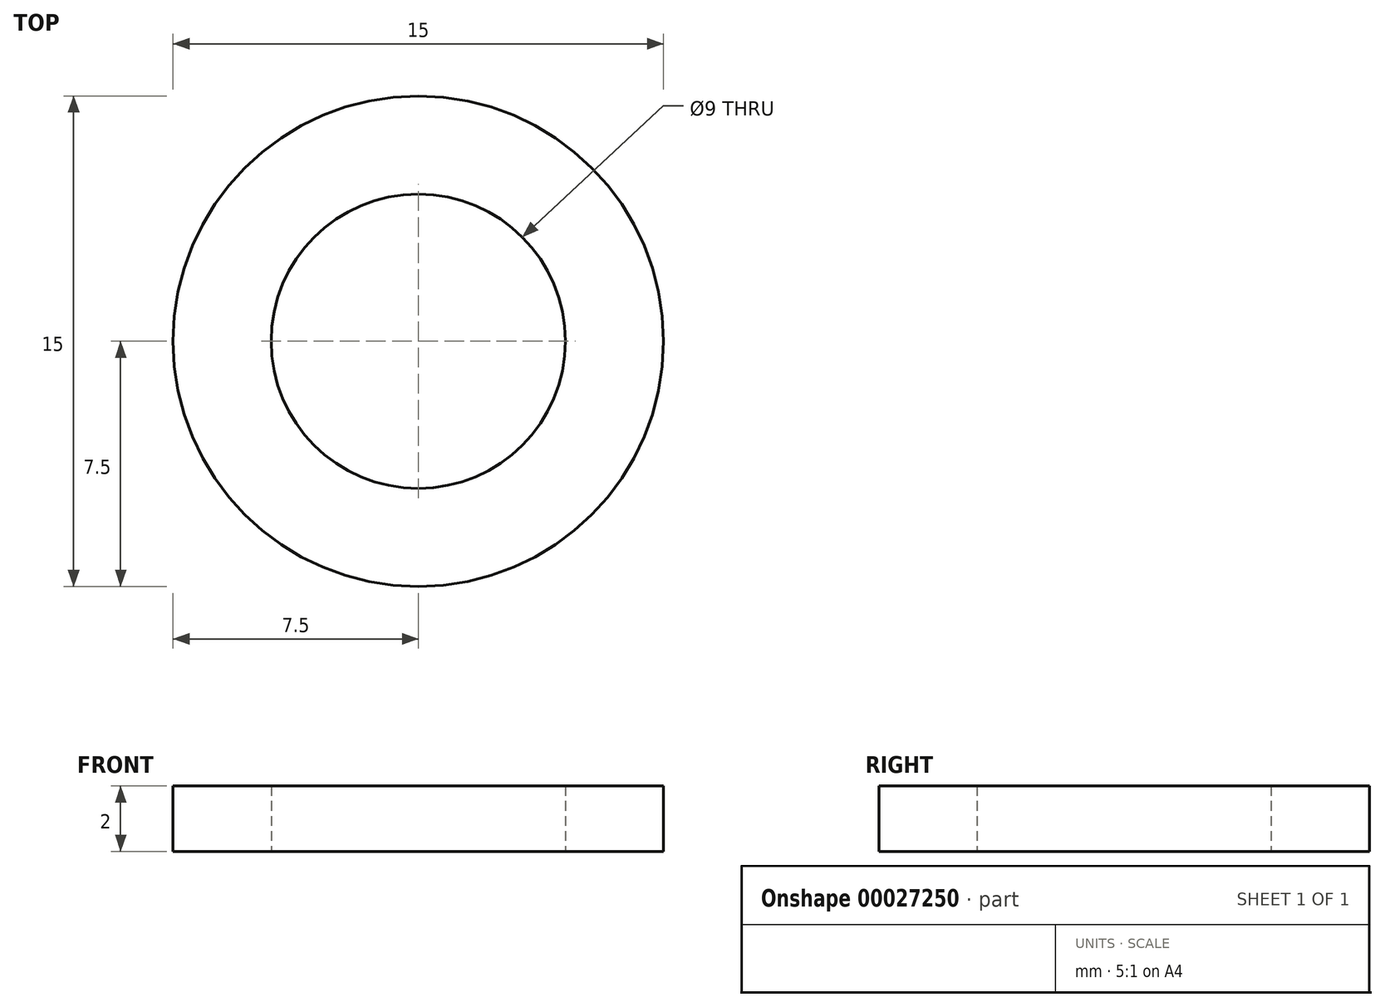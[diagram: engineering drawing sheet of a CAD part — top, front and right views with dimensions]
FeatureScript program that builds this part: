
annotation { "Feature Type Name" : "Feature", "Feature Type Description" : "" }
export const myFeature = defineFeature(function(context is Context, id is Id, definition is map)
    precondition{}
    {
        {
            var Q0;
            Q0=qCreatedBy(makeId("Top.planeOp"),FACE);
            var sketch = newSketch(context, id + "F0", { "sketchPlane" : qUnion([Q0])});
            skCircle(sketch, "E0", {"center": v(0, 0) * mm, "radius": 7.5 * mm});
            skCircle(sketch, "E1", {"center": v(0, 0) * mm, "radius": 4.5 * mm});
            skSolve(sketch);
        }
        {
            var Q0;
            Q0=makeQuery(id+"F0.imprint","IMPRINT",FACE,{"disambiguationData":[TD([[makeQuery(id+"F0.imprint","IMPRINT",EDGE,{"derivedFrom":sQuery(id+"F0.wireOp",EDGE,"E0")}),1.0]])]});
            extrude(context, id + "F1", {"entities" : qUnion([Q0]), "depth" : 2 * mm});
        }
    });
